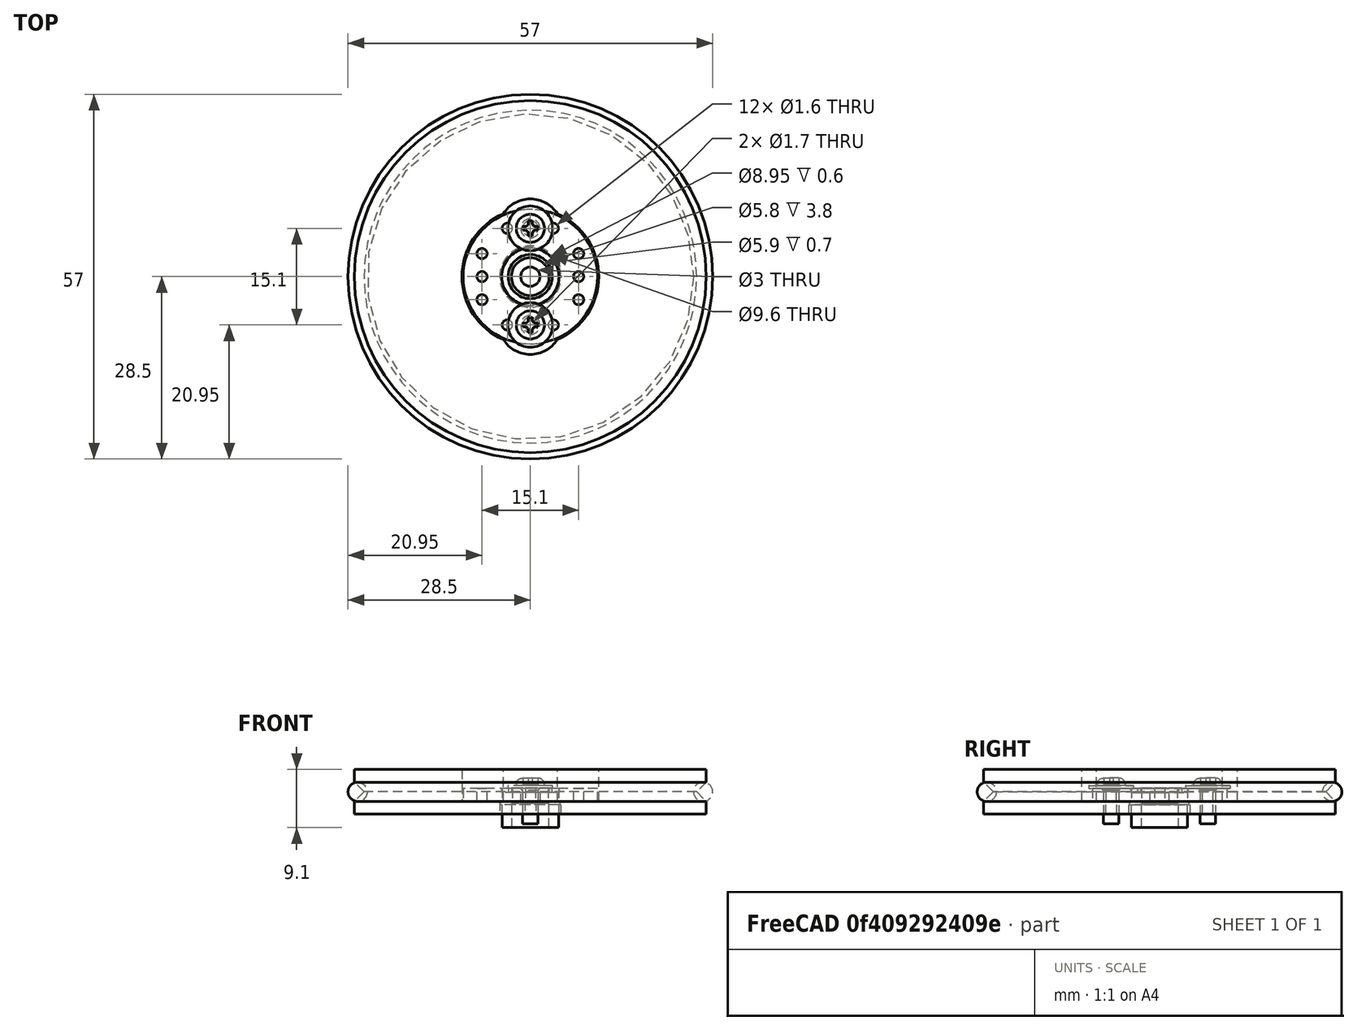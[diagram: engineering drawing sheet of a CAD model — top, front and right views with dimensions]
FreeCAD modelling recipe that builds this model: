
FCSTD DOCUMENT  (FreeCAD 0.14R3702 (Git))
Label: Renacuajo-wheel-small-rounded-horn-assembly
License: CC-BY 3.0
LicenseURL: http://creativecommons.org/licenses/by/3.0/
objects: Part::Feature×4, Part::Torus×1, Part::Compound×1
note: 6 computed .brp shape members not serialized (recipe doc carries the construction recipe); baked Part::Feature solids carry a one-line shape summary decoded from their .brp

FEATURE [Part::Feature] Pocket  label="small-rounded-horn"
  Placement = pos=(0,0,-1.5) rot=(0,0,1;0rad)
  shape: bbox 21 x 21 x 6.2 mm, 28 faces (baked)
FEATURE [Part::Feature] PolarPattern  label="renacuajo-wheel-small-rounded-horn-final"
  Placement = pos=(0,0,0) rot=(1,0,0;1.5708rad)
  shape: bbox 55 x 55 x 7 mm, 15 faces (baked)
FEATURE [Part::Feature] Chamfer001  label="screw1"
  Placement = pos=(0,-7.55,0.5) rot=(0,0,1;0rad)
  shape: bbox 7 x 7 x 7.14 mm, 33 faces (baked)
FEATURE [Part::Feature] Chamfer  label="screw2"
  Placement = pos=(0,7.55,0.5) rot=(0,0,1;0rad)
  shape: bbox 7 x 7 x 7.14 mm, 33 faces (baked)
FEATURE [Part::Torus] Torus  label="o-ring"
  Angle1 = -180
  Angle2 = 180
  Angle3 = 360
  Radius1 = 27
  Radius2 = 1.5
FEATURE [Part::Compound] Compound  label="Renacuajo-wheel-small-rounded-horn-assembly-final"
  Links = -> [Torus,Pocket,PolarPattern,Chamfer001,Chamfer]
